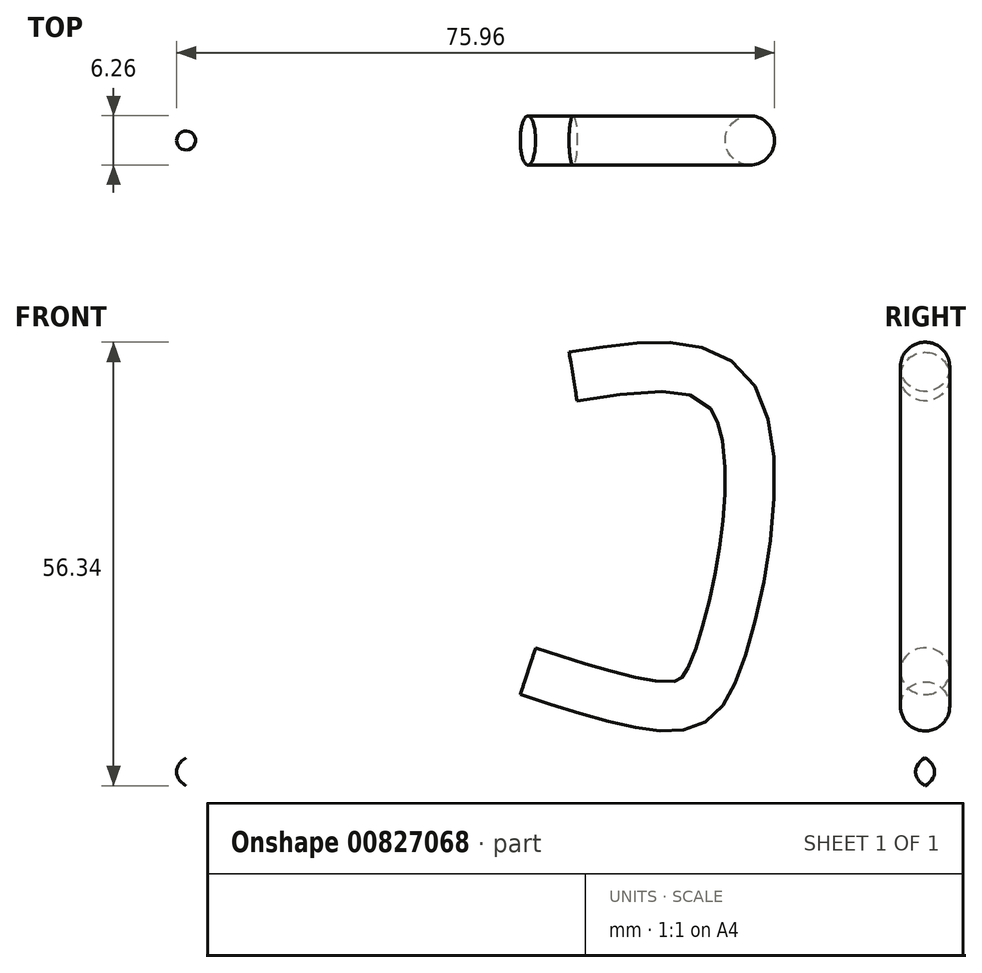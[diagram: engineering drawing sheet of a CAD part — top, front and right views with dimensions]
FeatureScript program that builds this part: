
annotation { "Feature Type Name" : "Feature", "Feature Type Description" : "" }
export const myFeature = defineFeature(function(context is Context, id is Id, definition is map)
    precondition{}
    {
        {
            var Q0;
            Q0=qCreatedBy(makeId("Front.planeOp"),FACE);
            var sketch = newSketch(context, id + "F0", { "sketchPlane" : qUnion([Q0])});
            skFitSpline(sketch, "E0", {"points": [v(0, 0) * mm, v(36.84, 5.04) * mm, v(45.9, 23.68) * mm, v(49.84, 62.32) * mm, v(48.13, 61.63) * mm, v(47.61, 50.18) * mm, v(41.29, 15.47) * mm, v(34.45, 7.1) * mm, v(0, 3.55) * mm, v(0, 0) * mm]});
            skLineSegment(sketch, "E1", {"start": v(0, 61.03) * mm, "end": v(0, -37.23) * mm});
            skSolve(sketch);
        }
        {
            var Q0;
            {var subQ0=sQuery(id+"F0.wireOp",EDGE,"E1");var subQ1=sQuery(id+"F0.wireOp",EDGE,"E0");var subQ2=makeQuery(id+"F0.imprint","INTERSECT",VERTEX,{"disambiguationData":[OD(0.0)],"derivedFrom":[subQ1,subQ0]});Q0=makeQuery(id+"F0.imprint","IMPRINT",FACE,{"disambiguationData":[TD([[makeQuery(id+"F0.imprint","IMPRINT",EDGE,{"disambiguationData":[TD([[subQ2,-1.0]])],"derivedFrom":subQ1}),1.0]])]});}
            var Q1;
            Q1=sQuery(id+"F0.wireOp",EDGE,"E1");
            revolve(context, id + "F1", {"surfaceOperationType" : NewSurfaceOperationType.NEW, "entities" : qUnion([Q0]), "axis" : qUnion([Q1]), "revolveType" : RevolveType.FULL});
        }
        {
            var Q0;
            Q0=qCreatedBy(makeId("Front.planeOp"),FACE);
            var sketch = newSketch(context, id + "F2", { "sketchPlane" : qUnion([Q0])});
            skFitSpline(sketch, "E2", {"points": [v(43.36, 14.3) * mm, v(62.2, 9.87) * mm, v(67.53, 15.2) * mm, v(69.75, 49.34) * mm, v(49.12, 52.23) * mm], "startDerivative": vector(88.15, -28.9) * mm, "endDerivative": vector(-98.6, -16.12) * mm});
            skSolve(sketch);
        }
        {
            var Q0;
            Q0=sQuery(id+"F2.wireOp",VERTEX,"E2.start");
            var Q1;
            Q1=sQuery(id+"F2.wireOp",EDGE,"E2");
            cPlane(context, id + "F3", {"entities" : qUnion([Q0, Q1]), "cplaneType" : CPlaneType.CURVE_POINT, "offset" : 25.4 * mm, "width" : 152.4 * mm, "height" : 152.4 * mm});
        }
        {
            var Q0;
            Q0=qCreatedBy(id+"F3.planeOp",FACE);
            var sketch = newSketch(context, id + "F4", { "sketchPlane" : qUnion([Q0])});
            skCircle(sketch, "E3", {"center": v(0, 27.35) * mm, "radius": 3.13 * mm});
            skSolve(sketch);
        }
        {
            var Q0;
            Q0=makeQuery(id+"F4.imprint","IMPRINT",FACE,{"disambiguationData":[TD([[makeQuery(id+"F4.imprint","IMPRINT",EDGE,{"derivedFrom":sQuery(id+"F4.wireOp",EDGE,"E3")}),1.0]])]});
            var Q1;
            Q1=sQuery(id+"F2.wireOp",EDGE,"E2");
            sweep(context, id + "F5", {"operationType" : NewBodyOperationType.ADD, "profiles" : qUnion([Q0]), "path" : qUnion([Q1])});
        }
    });
